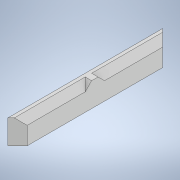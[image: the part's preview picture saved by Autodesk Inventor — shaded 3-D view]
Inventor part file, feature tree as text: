
AUTODESK INVENTOR PART (.ipt)
format: ipt  version: 2021 (Build 250183000, 183)  size: 126,464 bytes
history: native  units: in
note: dims shown in document units (in); Inventor stores cm internally (conversion verified against a paired STEP export)
features: extrude x3, sketch x3
ambient origin geometry x8: Origin, YZ Plane, XZ Plane, XY Plane, X Axis, Y Axis, Z Axis, Center Point
bodies: Solid1 (feature_tree)
feature tree (6):
  extrude  "Extrusion1"  Depth=0.2362in
  extrude  "Extrusion2"  Depth=0.5906in
  extrude  "Extrusion3"  Depth=0.2362in
  sketch  "Sketch1"  dims[d0=0.2362in d1=0.4331in]
  sketch  "Sketch2"  dims[d2=0.5906in d3=0.0787in]
  sketch  "Sketch3"  dims[d4=3.7795in d5=0.0in d7=0.2362in d8=0.2362in d9=1.658in d10=0.0in d11=0.2362in d12=0.2362in d13=0.0787in d14=0.0787in d15=0.2362in d16=0.0in]
